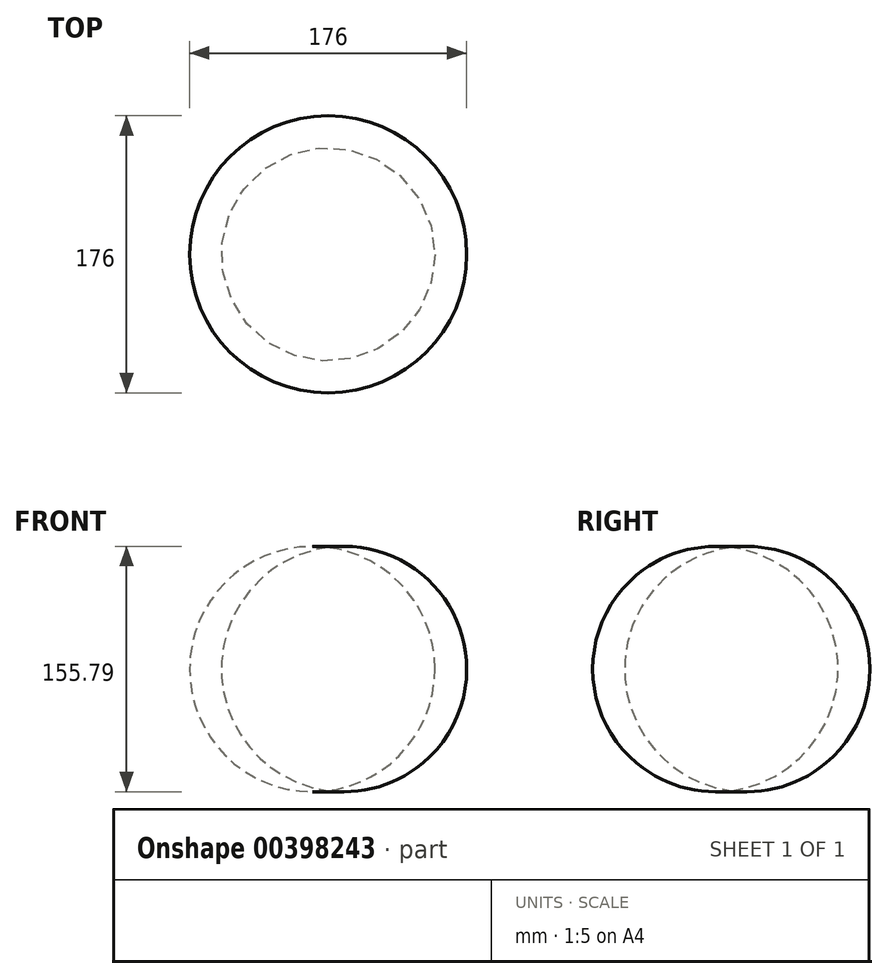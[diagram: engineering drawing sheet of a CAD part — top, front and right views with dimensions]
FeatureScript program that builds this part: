
annotation { "Feature Type Name" : "Feature", "Feature Type Description" : "" }
export const myFeature = defineFeature(function(context is Context, id is Id, definition is map)
    precondition{}
    {
        {
            var Q0;
            Q0=qCreatedBy(makeId("Front.planeOp"),FACE);
            var sketch = newSketch(context, id + "F0", { "sketchPlane" : qUnion([Q0])});
            skLineSegment(sketch, "E0", {"start": v(0, 82.91) * mm, "end": v(0, -71.56) * mm});
            skArc(sketch, "E1", {"start": v(0, -71.56) * mm, "mid": v(67.8, 5.68) * mm, "end": v(0, 82.91) * mm});
            skLineSegment(sketch, "E2.bottom", {"start": v(-18.46, 36.5) * mm, "end": v(0, 36.5) * mm});
            skLineSegment(sketch, "E2.top", {"start": v(-18.46, 19.04) * mm, "end": v(0, 19.04) * mm});
            skLineSegment(sketch, "E2.left", {"start": v(-18.46, 36.5) * mm, "end": v(-18.46, 19.04) * mm});
            skSolve(sketch);
        }
        {
            var Q0;
            Q0=makeQuery(id+"F0.imprint","IMPRINT",FACE,{"disambiguationData":[TD([[makeQuery(id+"F0.imprint","IMPRINT",EDGE,{"derivedFrom":sQuery(id+"F0.wireOp",EDGE,"E0")}),1.0]])]});
            var Q1;
            Q1=sQuery(id+"F0.wireOp",EDGE,"E0");
            revolve(context, id + "F1", {"entities" : qUnion([Q0]), "axis" : qUnion([Q1]), "revolveType" : RevolveType.SYMMETRIC, "oppositeDirection" : true, "angle" : 360 * degree});
        }
    });
